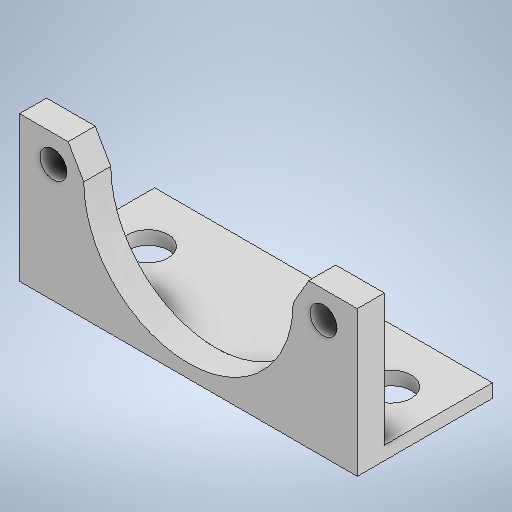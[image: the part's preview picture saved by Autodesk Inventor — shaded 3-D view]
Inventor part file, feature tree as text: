
AUTODESK INVENTOR PART (.ipt)
format: ipt  version: 2025.3 (Build 293356000, 356)  size: 269,312 bytes
history: native  units: mm
features: sketch x3, extrude x2, other x1, hole x1
ambient origin geometry x8: Origin, YZ Plane, XZ Plane, XY Plane, X Axis, Y Axis, Z Axis, Center Point
bodies: Body1 (feature_tree)
feature tree (7):
  other  "ソリッド1"
  extrude  "押し出し1"  Depth=25.0mm
  extrude  "押し出し2"  Depth=10.0mm
  hole  "穴1"  [1 undecoded]
  sketch  "スケッチ1"
  sketch  "スケッチ2"
  sketch  "スケッチ4"
note: 1 required parameter value undecoded (feature->parameter linkage not recoverable at this tier; creation-order binding heuristic only, values carry confidence <= 0.55)
